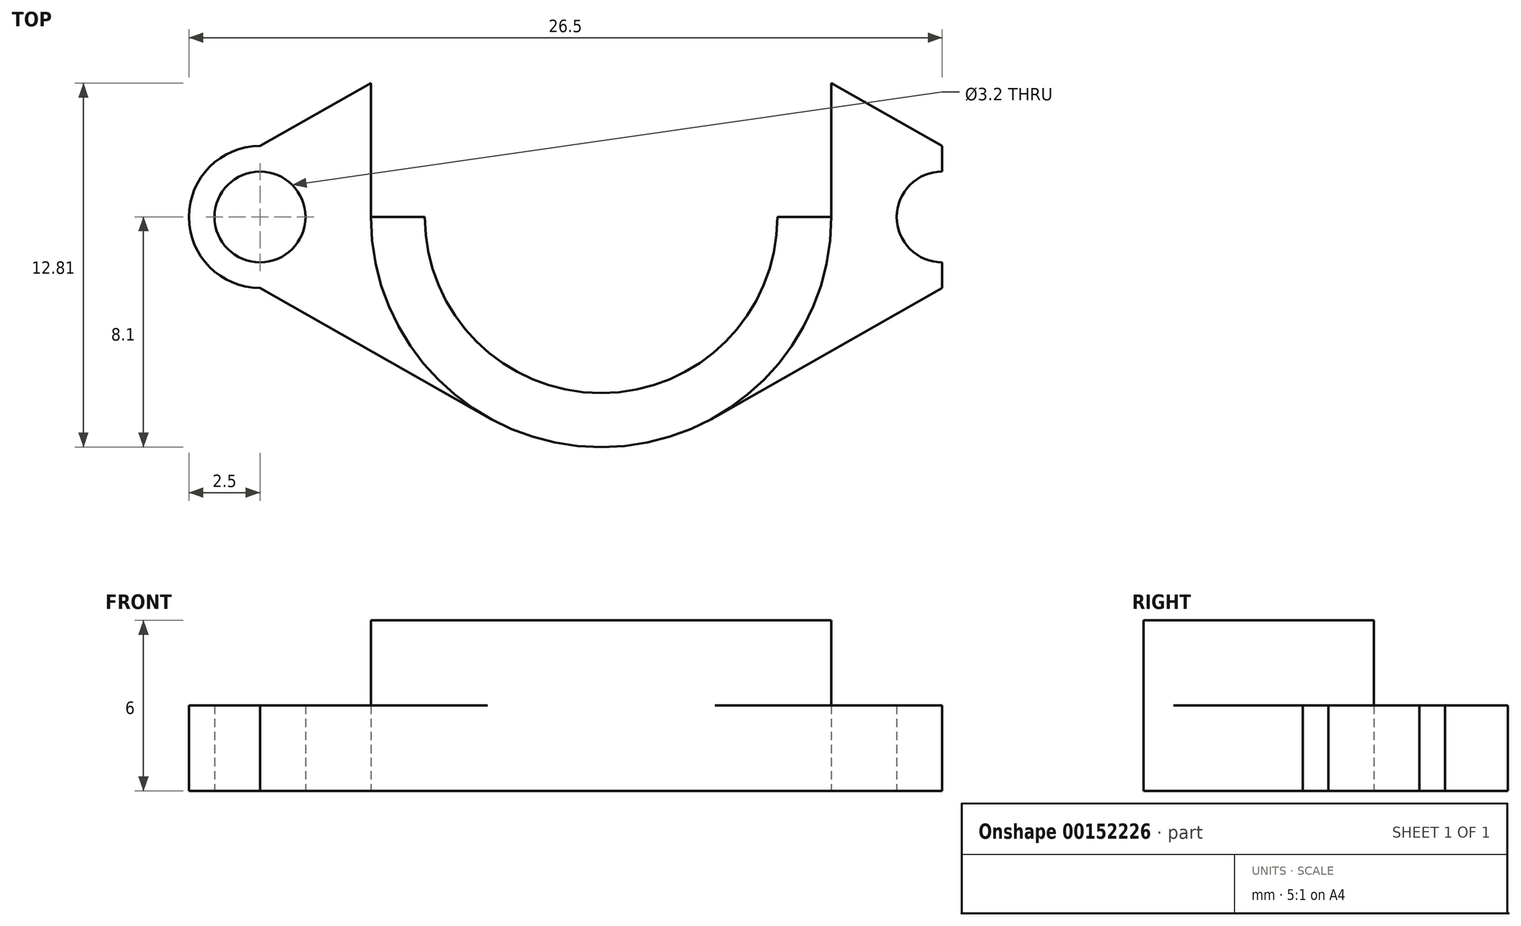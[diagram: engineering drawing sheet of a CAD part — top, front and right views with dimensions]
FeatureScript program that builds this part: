
annotation { "Feature Type Name" : "Feature", "Feature Type Description" : "" }
export const myFeature = defineFeature(function(context is Context, id is Id, definition is map)
    precondition{}
    {
        {
            var Q0;
            Q0=qCreatedBy(makeId("Top.planeOp"),FACE);
            var sketch = newSketch(context, id + "F0", { "sketchPlane" : qUnion([Q0])});
            skCircle(sketch, "E0", {"center": v(0, 0) * mm, "radius": 6.2 * mm});
            skCircle(sketch, "E1", {"center": v(0, 0) * mm, "radius": 8.1 * mm});
            skLineSegment(sketch, "E2", {"start": v(0, 0) * mm, "end": v(12, 0) * mm});
            skLineSegment(sketch, "E3", {"start": v(0, 0) * mm, "end": v(-12, 0) * mm});
            skCircle(sketch, "E4", {"center": v(-12, 0) * mm, "radius": 1.6 * mm});
            skCircle(sketch, "E5", {"center": v(12, 0) * mm, "radius": 1.6 * mm});
            skCircle(sketch, "E6", {"center": v(12, 0) * mm, "radius": 2.5 * mm});
            skCircle(sketch, "E7", {"center": v(-12, 0) * mm, "radius": 2.5 * mm});
            skLineSegment(sketch, "E8", {"start": v(12, 0) * mm, "end": v(12, 2.5) * mm});
            skLineSegment(sketch, "E9", {"start": v(12, 2.5) * mm, "end": v(12, -2.5) * mm});
            skLineSegment(sketch, "E10", {"start": v(12, -2.5) * mm, "end": v(4, -7.04) * mm});
            skLineSegment(sketch, "E11", {"start": v(12, 2.5) * mm, "end": v(4, 7.04) * mm});
            skLineSegment(sketch, "E12", {"start": v(-12, 0) * mm, "end": v(-12, -2.5) * mm});
            skLineSegment(sketch, "E13", {"start": v(-12, -2.5) * mm, "end": v(-12, 2.5) * mm});
            skLineSegment(sketch, "E14", {"start": v(-12, 2.5) * mm, "end": v(-4, 7.04) * mm});
            skLineSegment(sketch, "E15", {"start": v(-12, -2.5) * mm, "end": v(-4, -7.04) * mm});
            skLineSegment(sketch, "E16", {"start": v(8.1, 0) * mm, "end": v(8.1, 8.7) * mm});
            skLineSegment(sketch, "E17", {"start": v(-8.1, 0) * mm, "end": v(-8.1, 9.9) * mm});
            skSolve(sketch);
        }
        {
            var Q0;
            {var subQ2=sQuery(id+"F0.wireOp",EDGE,"E2");var subQ5=sQuery(id+"F0.wireOp",EDGE,"E0");var subQ9=makeQuery(id+"F0.imprint","INTERSECT",VERTEX,{"derivedFrom":[subQ5,subQ2]});Q0=makeQuery(id+"F0.imprint","IMPRINT",FACE,{"disambiguationData":[TD([[makeQuery(id+"F0.imprint","IMPRINT",EDGE,{"disambiguationData":[TD([[subQ9,1.0]])],"derivedFrom":subQ5}),-1.0]])]});}
            extrude(context, id + "F1", {"entities" : qUnion([Q0]), "depth" : 6 * mm});
        }
        {
            var Q0;
            {var subQ0=sQuery(id+"F0.wireOp",EDGE,"E10");Q0=makeQuery(id+"F0.imprint","IMPRINT",FACE,{"disambiguationData":[TD([[makeQuery(id+"F0.imprint","IMPRINT",EDGE,{"derivedFrom":subQ0}),-1.0]])]});}
            var Q1;
            {var subQ0=sQuery(id+"F0.wireOp",EDGE,"E6");var subQ1=sQuery(id+"F0.wireOp",EDGE,"E2");var subQ2=makeQuery(id+"F0.imprint","INTERSECT",VERTEX,{"derivedFrom":[subQ1,subQ0]});Q1=makeQuery(id+"F0.imprint","IMPRINT",FACE,{"disambiguationData":[TD([[makeQuery(id+"F0.imprint","IMPRINT",EDGE,{"disambiguationData":[TD([[subQ2,-1.0]])],"derivedFrom":subQ1}),-1.0]])]});}
            var Q2;
            {var subQ0=sQuery(id+"F0.wireOp",EDGE,"E9");var subQ1=sQuery(id+"F0.wireOp",EDGE,"E5");var subQ2=makeQuery(id+"F0.imprint","INTERSECT",VERTEX,{"disambiguationData":[OD(0.0)],"derivedFrom":[subQ1,subQ0]});Q2=makeQuery(id+"F0.imprint","IMPRINT",FACE,{"disambiguationData":[TD([[makeQuery(id+"F0.imprint","IMPRINT",EDGE,{"disambiguationData":[TD([[subQ2,1.0]])],"derivedFrom":subQ1}),-1.0]])]});}
            var Q3;
            {var subQ0=sQuery(id+"F0.wireOp",EDGE,"E15");Q3=makeQuery(id+"F0.imprint","IMPRINT",FACE,{"disambiguationData":[TD([[makeQuery(id+"F0.imprint","IMPRINT",EDGE,{"derivedFrom":subQ0}),1.0]])]});}
            var Q4;
            {var subQ0=sQuery(id+"F0.wireOp",EDGE,"E6");var subQ1=sQuery(id+"F0.wireOp",EDGE,"E2");var subQ2=makeQuery(id+"F0.imprint","INTERSECT",VERTEX,{"derivedFrom":[subQ1,subQ0]});Q4=makeQuery(id+"F0.imprint","IMPRINT",FACE,{"disambiguationData":[TD([[makeQuery(id+"F0.imprint","IMPRINT",EDGE,{"disambiguationData":[TD([[subQ2,-1.0]])],"derivedFrom":subQ1}),1.0]])]});}
            var Q5;
            {var subQ0=sQuery(id+"F0.wireOp",EDGE,"E7");var subQ1=sQuery(id+"F0.wireOp",EDGE,"E3");var subQ2=makeQuery(id+"F0.imprint","INTERSECT",VERTEX,{"derivedFrom":[subQ1,subQ0]});Q5=makeQuery(id+"F0.imprint","IMPRINT",FACE,{"disambiguationData":[TD([[makeQuery(id+"F0.imprint","IMPRINT",EDGE,{"disambiguationData":[TD([[subQ2,-1.0]])],"derivedFrom":subQ1}),1.0]])]});}
            var Q6;
            {var subQ0=sQuery(id+"F0.wireOp",EDGE,"E13");var subQ1=sQuery(id+"F0.wireOp",EDGE,"E4");var subQ2=makeQuery(id+"F0.imprint","INTERSECT",VERTEX,{"disambiguationData":[OD(0.0)],"derivedFrom":[subQ1,subQ0]});Q6=makeQuery(id+"F0.imprint","IMPRINT",FACE,{"disambiguationData":[TD([[makeQuery(id+"F0.imprint","IMPRINT",EDGE,{"disambiguationData":[TD([[subQ2,-1.0]])],"derivedFrom":subQ1}),-1.0]])]});}
            var Q7;
            {var subQ0=sQuery(id+"F0.wireOp",EDGE,"E7");var subQ1=sQuery(id+"F0.wireOp",EDGE,"E3");var subQ2=makeQuery(id+"F0.imprint","INTERSECT",VERTEX,{"derivedFrom":[subQ1,subQ0]});Q7=makeQuery(id+"F0.imprint","IMPRINT",FACE,{"disambiguationData":[TD([[makeQuery(id+"F0.imprint","IMPRINT",EDGE,{"disambiguationData":[TD([[subQ2,-1.0]])],"derivedFrom":subQ1}),-1.0]])]});}
            var Q8;
            {var subQ1=sQuery(id+"F0.wireOp",EDGE,"E3");var subQ3=sQuery(id+"F0.wireOp",EDGE,"E7");var subQ4=makeQuery(id+"F0.imprint","INTERSECT",VERTEX,{"derivedFrom":[subQ1,subQ3]});Q8=makeQuery(id+"F0.imprint","IMPRINT",FACE,{"disambiguationData":[TD([[makeQuery(id+"F0.imprint","IMPRINT",EDGE,{"disambiguationData":[TD([[subQ4,1.0]])],"derivedFrom":subQ1}),-1.0]])]});}
            var Q9;
            {var subQ1=sQuery(id+"F0.wireOp",EDGE,"E2");var subQ3=sQuery(id+"F0.wireOp",EDGE,"E6");var subQ4=makeQuery(id+"F0.imprint","INTERSECT",VERTEX,{"derivedFrom":[subQ1,subQ3]});Q9=makeQuery(id+"F0.imprint","IMPRINT",FACE,{"disambiguationData":[TD([[makeQuery(id+"F0.imprint","IMPRINT",EDGE,{"disambiguationData":[TD([[subQ4,1.0]])],"derivedFrom":subQ1}),1.0]])]});}
            extrude(context, id + "F2", {"entities" : qUnion([Q0, Q1, Q2, Q3, Q4, Q5, Q6, Q7, Q8, Q9]), "operationType" : NewBodyOperationType.ADD, "depth" : 3 * mm});
        }
    });
